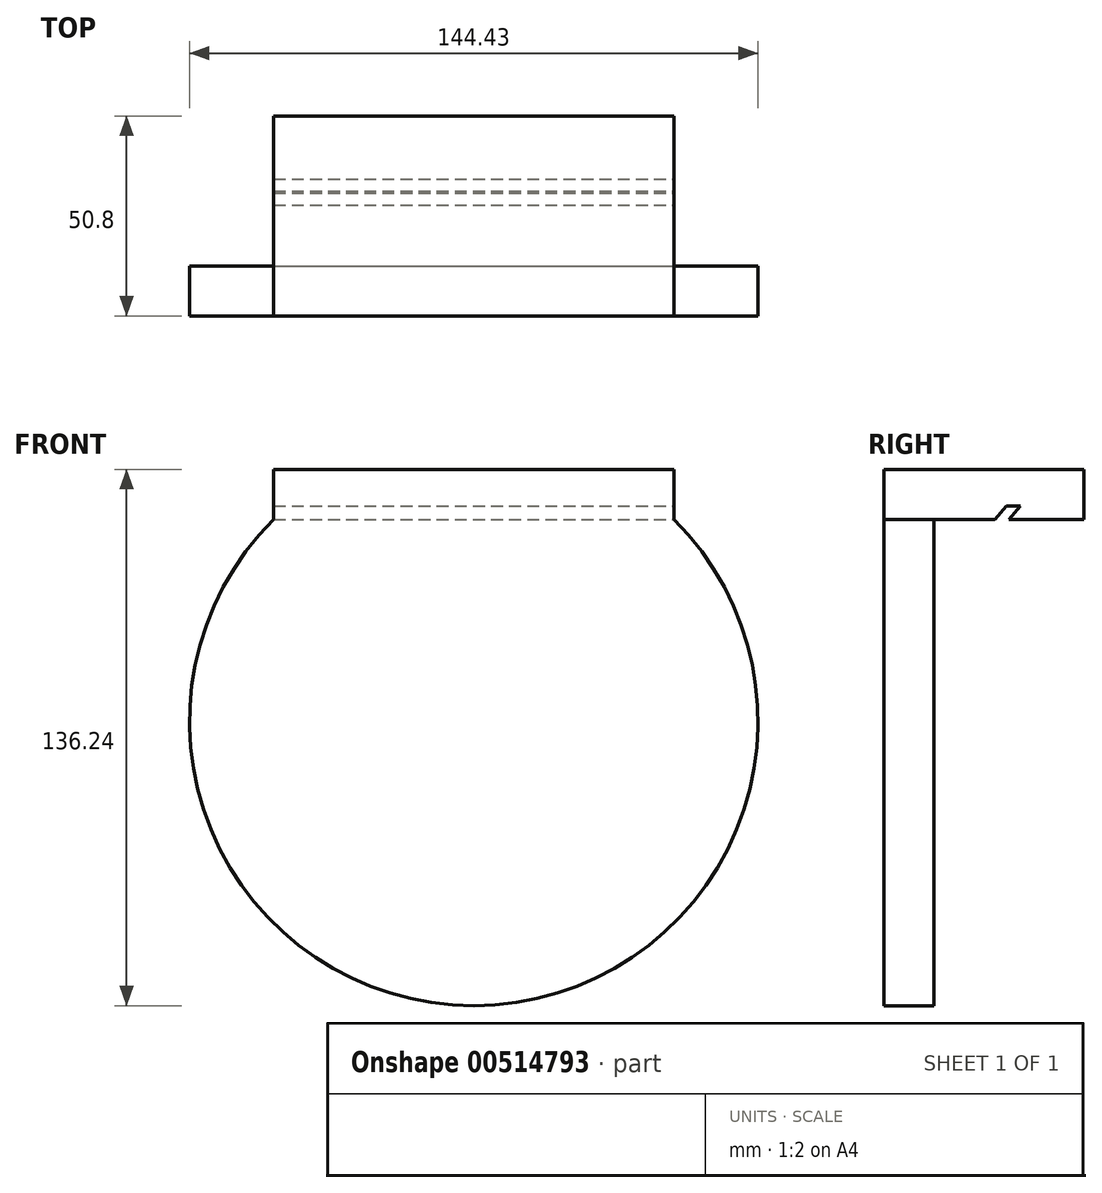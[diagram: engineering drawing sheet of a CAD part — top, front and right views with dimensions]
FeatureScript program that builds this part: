
annotation { "Feature Type Name" : "Feature", "Feature Type Description" : "" }
export const myFeature = defineFeature(function(context is Context, id is Id, definition is map)
    precondition{}
    {
        {
            var Q0;
            Q0=qCreatedBy(makeId("Top.planeOp"),FACE);
            var sketch = newSketch(context, id + "F0", { "sketchPlane" : qUnion([Q0])});
            skLineSegment(sketch, "E0.bottom", {"start": v(-56.63, -20.35) * mm, "end": v(44.97, -20.35) * mm});
            skLineSegment(sketch, "E0.top", {"start": v(-56.63, 30.45) * mm, "end": v(44.97, 30.45) * mm});
            skLineSegment(sketch, "E0.left", {"start": v(-56.63, -20.35) * mm, "end": v(-56.63, 30.45) * mm});
            skLineSegment(sketch, "E0.right", {"start": v(44.97, -20.35) * mm, "end": v(44.97, 30.45) * mm});
            skSolve(sketch);
        }
        {
            var Q0;
            Q0=makeQuery(id+"F0.imprint","IMPRINT",FACE,{"disambiguationData":[TD([[makeQuery(id+"F0.imprint","IMPRINT",EDGE,{"derivedFrom":sQuery(id+"F0.wireOp",EDGE,"E0.bottom")}),1.0]])]});
            extrude(context, id + "F1", {"entities" : qUnion([Q0]), "depth" : 12.7 * mm, "offsetDistance" : 25.4 * mm});
        }
        {
            var Q0;
            Q0=makeQuery(id+"F1.opExtrude","SWEPT_FACE",FACE,{"disambiguationData":[OSD([sQuery(id+"F0.wireOp",EDGE,"E0.right")])]});
            var sketch = newSketch(context, id + "F2", { "sketchPlane" : qUnion([Q0])});
            skLineSegment(sketch, "E1", {"start": v(11.34, 0) * mm, "end": v(14.36, 3.43) * mm});
            skLineSegment(sketch, "E2", {"start": v(14.36, 3.43) * mm, "end": v(10.8, 3.43) * mm});
            skLineSegment(sketch, "E3", {"start": v(10.8, 3.43) * mm, "end": v(7.78, 0) * mm});
            skSolve(sketch);
        }
        {
            var Q0;
            {var subQ0=sQuery(id+"F2.wireOp",EDGE,"E1");Q0=makeQuery(id+"F2.imprint","IMPRINT",FACE,{"disambiguationData":[TD([[makeQuery(id+"F2.imprint","IMPRINT",EDGE,{"derivedFrom":subQ0}),1.0]])]});}
            extrude(context, id + "F3", {"entities" : qUnion([Q0]), "operationType" : NewBodyOperationType.REMOVE, "oppositeDirection" : true, "depth" : 101.6 * mm, "offsetDistance" : 25.4 * mm});
        }
        {
            var Q0;
            Q0=makeQuery(id+"F1.opExtrude","SWEPT_FACE",FACE,{"disambiguationData":[OSD([sQuery(id+"F0.wireOp",EDGE,"E0.bottom")])]});
            var sketch = newSketch(context, id + "F4", { "sketchPlane" : qUnion([Q0])});
            skCircle(sketch, "E4", {"center": v(-5.83, -51.32) * mm, "radius": 72.21 * mm});
            skPoint(sketch, "E4.first.point", {"position": v(44.97, 0) * mm});
            skPoint(sketch, "E4.second.point", {"position": v(-56.63, 0) * mm});
            skPoint(sketch, "E4.third.point", {"position": v(27.09, -115.6) * mm});
            skSolve(sketch);
        }
        {
            var Q0;
            {var subQ1=sQuery(id+"F0.wireOp",EDGE,"E0.bottom");var subQ2=makeQuery(id+"F1.opExtrude","CAP_EDGE",EDGE,{"disambiguationData":[OSD([subQ1])],"isStart":true});Q0=makeQuery(id+"F4.imprint","IMPRINT",FACE,{"disambiguationData":[TD([[makeQuery(id+"F4.imprint","IMPRINT",EDGE,{"derivedFrom":subQ2}),-1.0]])]});}
            extrude(context, id + "F5", {"entities" : qUnion([Q0]), "operationType" : NewBodyOperationType.ADD, "oppositeDirection" : true, "depth" : 12.7 * mm, "offsetDistance" : 25.4 * mm});
        }
    });
